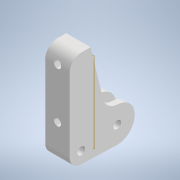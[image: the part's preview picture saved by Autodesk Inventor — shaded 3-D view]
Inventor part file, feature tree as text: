
AUTODESK INVENTOR PART (.ipt)
format: ipt  version: 2022.2 (Build 262287000, 287)  size: 335,872 bytes
history: native  units: mm
features: sketch x7, extrude x5, other x4, projected_geometry x3, plane x2, hole x1, fillet x1, reference x1
ambient origin geometry x8: Origin, YZ Plane, XZ Plane, XY Plane, X Axis, Y Axis, Z Axis, Center Point
bodies: Solid1 (feature_tree)
feature tree (24):
  other  "Motor.ipt"
  extrude  "Extrusion1"  Depth=3.3mm
  extrude  "Extrusion2"  Depth=10.0mm
  extrude  "Extrusion3"  Depth=5.0mm
  plane  "Work Plane1"
  sketch  "Sketch5"  dims[d7=15.0mm d8=3.3mm d13=2.5mm d14=0.0mm]
  hole  "Hole1"  [1 undecoded]
  fillet  "Fillet1"  Radius=2.5mm
  extrude  "Extrusion5"  Depth=2.5mm TaperAngle=0.0deg
  plane  "Work Plane2"
  extrude  "Extrusion6"  Depth=4.0mm
  sketch  "Sketch1"  dims[d0=16.0mm d1=3.3mm]
  sketch  "Sketch2"  dims[d2=10.0mm d3=15.500005mm]
  projected_geometry  "Projected Loop1"
  sketch  "Sketch3"  dims[d4=2.000005mm d6=5.0mm]
  projected_geometry  "Projected Loop2"
  projected_geometry  "Projected Loop3"
  sketch  "Sketch6"  dims[d15=5.5mm d16=0.0mm d20=2.5mm d21=0.0mm]
  sketch  "Sketch7"  dims[d28=3.0mm d29=6.0mm d30=4.0mm d31=2.0mm d32=90.0deg d33=8.0mm d34=20.594885mm d35=4.0mm]
  reference  "Reference1"
  sketch  "Sketch9"  dims[d36=2.0mm d37=3.0mm d39=32.0mm d40=0.0mm d41=0.0mm d42=-10.0mm d43=7.2mm d44=4.0mm d45=0.0mm]
  other  "<userpath>\Documents\Inventor\Wire Bender\Assembly.iam"
  other  "Assembly.iam"
  other  "Feed Motor Mount:1"
note: 1 required parameter value undecoded (feature->parameter linkage not recoverable at this tier; creation-order binding heuristic only, values carry confidence <= 0.55)
